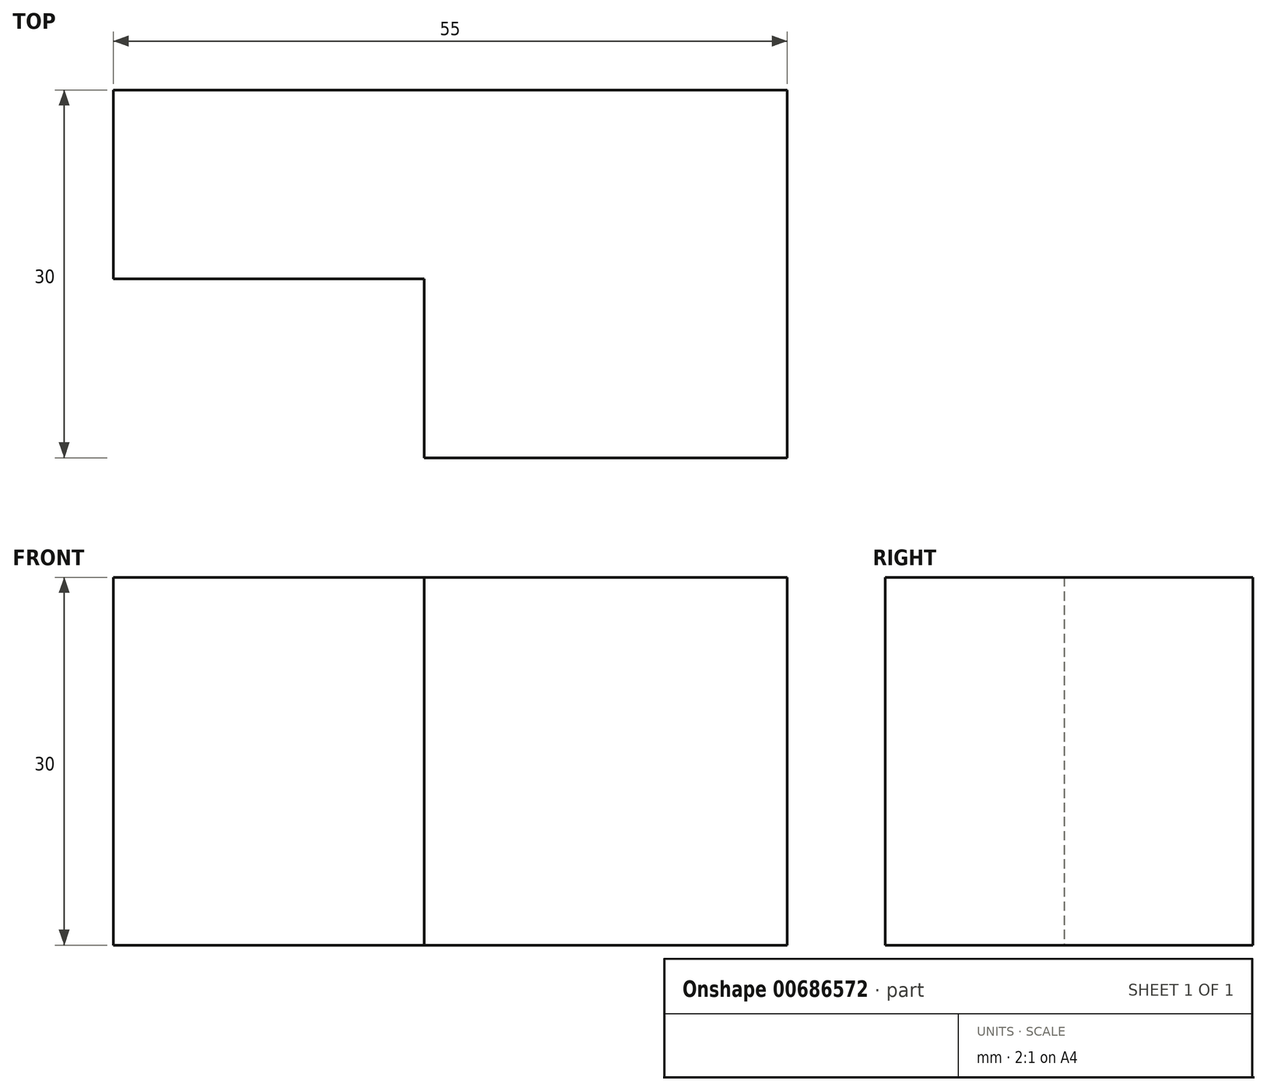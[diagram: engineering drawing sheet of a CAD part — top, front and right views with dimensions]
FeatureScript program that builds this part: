
annotation { "Feature Type Name" : "Feature", "Feature Type Description" : "" }
export const myFeature = defineFeature(function(context is Context, id is Id, definition is map)
    precondition{}
    {
        {
            var Q0;
            Q0=qCreatedBy(makeId("Top.planeOp"),FACE);
            var sketch = newSketch(context, id + "F0", { "sketchPlane" : qUnion([Q0])});
            skLineSegment(sketch, "E0.bottom", {"start": v(-27.5, 15) * mm, "end": v(27.5, 15) * mm});
            skLineSegment(sketch, "E0.top", {"start": v(-27.5, -15) * mm, "end": v(27.5, -15) * mm});
            skLineSegment(sketch, "E0.left", {"start": v(-27.5, 15) * mm, "end": v(-27.5, -15) * mm});
            skLineSegment(sketch, "E0.right", {"start": v(27.5, 15) * mm, "end": v(27.5, -15) * mm});
            skPoint(sketch, "E0.middle", {"position": v(0, 0) * mm});
            skSolve(sketch);
        }
        {
            var Q0;
            Q0=makeQuery(id+"F0.imprint","IMPRINT",FACE,{"disambiguationData":[TD([[makeQuery(id+"F0.imprint","IMPRINT",EDGE,{"derivedFrom":sQuery(id+"F0.wireOp",EDGE,"E0.bottom")}),-1.0]])]});
            extrude(context, id + "F1", {"entities" : qUnion([Q0]), "depth" : 30 * mm, "offsetDistance" : 25.4 * mm});
        }
        {
            var Q0;
            Q0=makeQuery(id+"F1.opExtrude","CAP_FACE",FACE,{"disambiguationData":[OSD([sQuery(id+"F0.wireOp",EDGE,"E0.bottom"),sQuery(id+"F0.wireOp",EDGE,"E0.top"),sQuery(id+"F0.wireOp",EDGE,"E0.left"),sQuery(id+"F0.wireOp",EDGE,"E0.right")])],"isStart":true});
            var sketch = newSketch(context, id + "F2", { "sketchPlane" : qUnion([Q0])});
            skLineSegment(sketch, "E1.bottom", {"start": v(-2.12, 15) * mm, "end": v(-32.4, 15) * mm});
            skLineSegment(sketch, "E1.top", {"start": v(-2.12, 0.4) * mm, "end": v(-32.4, 0.4) * mm});
            skLineSegment(sketch, "E1.left", {"start": v(-2.12, 15) * mm, "end": v(-2.12, 0.4) * mm});
            skLineSegment(sketch, "E1.right", {"start": v(-32.4, 15) * mm, "end": v(-32.4, 0.4) * mm});
            skPoint(sketch, "E1.middle", {"position": v(-17.26, 7.7) * mm});
            skSolve(sketch);
        }
        {
            var Q0;
            Q0 = qSketchRegion(id + "F2", true);
            extrude(context, id + "F3", {"entities" : qUnion([Q0]), "operationType" : NewBodyOperationType.REMOVE, "oppositeDirection" : true, "depth" : 30 * mm, "offsetDistance" : 25.4 * mm});
        }
    });
